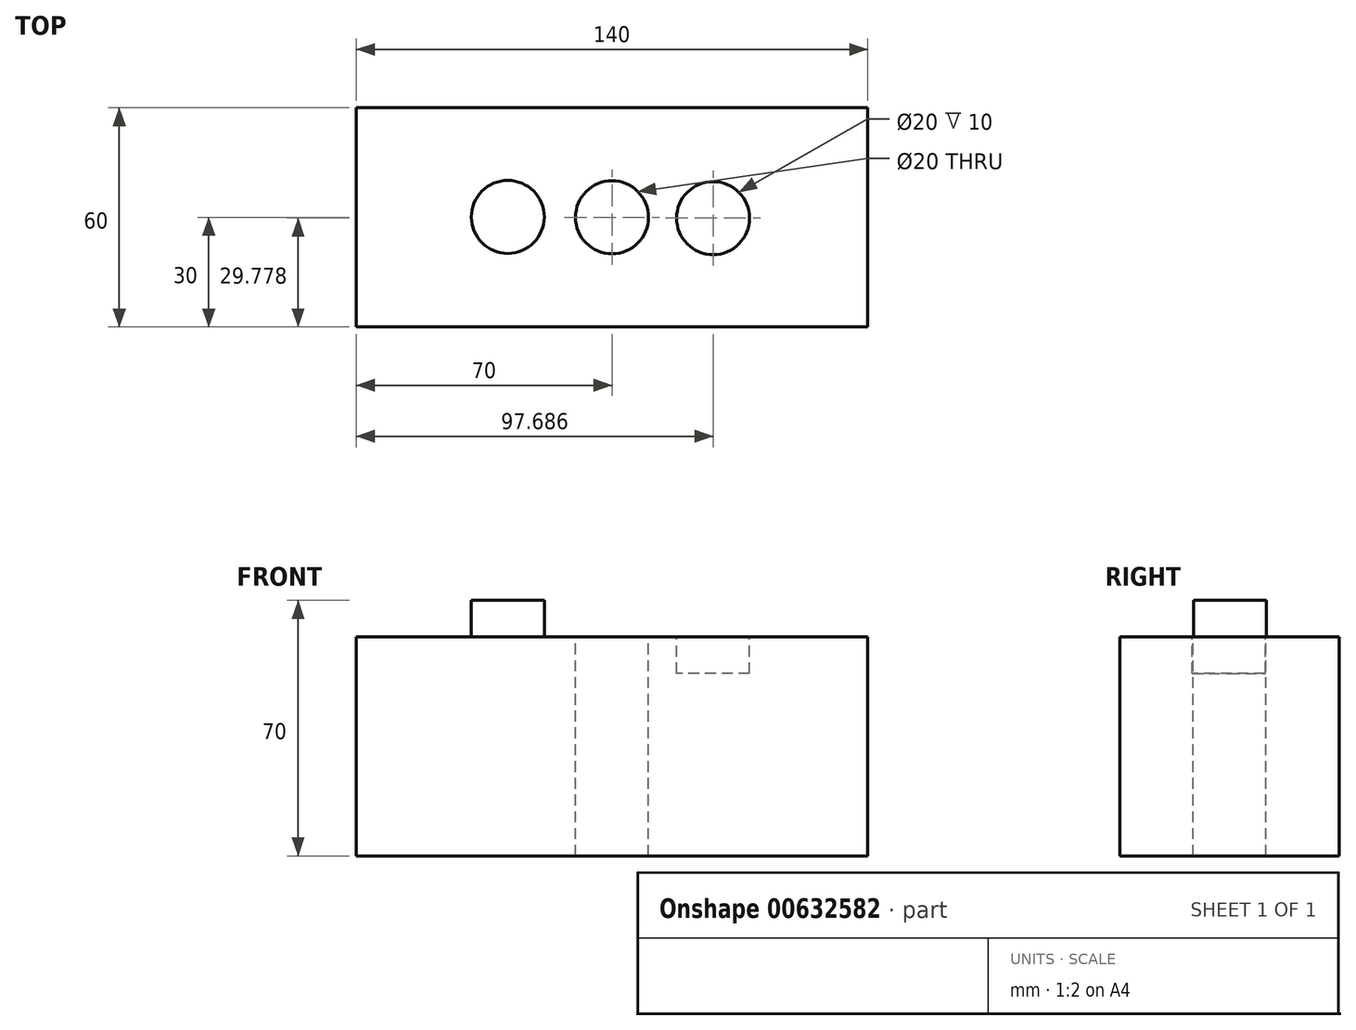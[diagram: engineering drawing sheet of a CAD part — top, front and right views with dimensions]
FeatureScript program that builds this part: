
annotation { "Feature Type Name" : "Feature", "Feature Type Description" : "" }
export const myFeature = defineFeature(function(context is Context, id is Id, definition is map)
    precondition{}
    {
        {
            var Q0;
            Q0=qCreatedBy(makeId("Top.planeOp"),FACE);
            var sketch = newSketch(context, id + "F0", { "sketchPlane" : qUnion([Q0])});
            skLineSegment(sketch, "E0.bottom", {"start": v(-70, 30) * mm, "end": v(70, 30) * mm});
            skLineSegment(sketch, "E0.top", {"start": v(-70, -30) * mm, "end": v(70, -30) * mm});
            skLineSegment(sketch, "E0.left", {"start": v(-70, 30) * mm, "end": v(-70, -30) * mm});
            skLineSegment(sketch, "E0.right", {"start": v(70, 30) * mm, "end": v(70, -30) * mm});
            skPoint(sketch, "E0.middle", {"position": v(0, 0) * mm});
            skSolve(sketch);
        }
        {
            var Q0;
            Q0 = qSketchRegion(id + "F0", true);
            extrude(context, id + "F1", {"entities" : qUnion([Q0]), "depth" : 60 * mm, "offsetDistance" : 25 * mm});
        }
        {
            var Q0;
            Q0=makeQuery(id+"F1.opExtrude","CAP_FACE",FACE,{"disambiguationData":[OSD([sQuery(id+"F0.wireOp",EDGE,"E0.bottom"),sQuery(id+"F0.wireOp",EDGE,"E0.top"),sQuery(id+"F0.wireOp",EDGE,"E0.left"),sQuery(id+"F0.wireOp",EDGE,"E0.right")])],"isStart":false});
            var sketch = newSketch(context, id + "F2", { "sketchPlane" : qUnion([Q0])});
            skLineSegment(sketch, "E1", {"start": v(-70, 0) * mm, "end": v(-49.87, 0) * mm});
            skPoint(sketch, "E1.endSnap0", {"position": v(-70, 0) * mm});
            skLineSegment(sketch, "E2", {"start": v(70, 0) * mm, "end": v(49, 0) * mm});
            skPoint(sketch, "E2.endSnap0", {"position": v(70, 0) * mm});
            skSolve(sketch);
        }
        {
            var Q0;
            {var subQ3=makeQuery(id+"F1.opExtrude","CAP_EDGE",EDGE,{"disambiguationData":[OSD([sQuery(id+"F0.wireOp",EDGE,"E0.bottom")])],"isStart":false});Q0=makeQuery(id+"F2.imprint","IMPRINT",FACE,{"disambiguationData":[TD([[makeQuery(id+"F2.imprint","IMPRINT",EDGE,{"derivedFrom":subQ3}),-1.0]])]});}
            var sketch = newSketch(context, id + "F3", { "sketchPlane" : qUnion([Q0])});
            skCircle(sketch, "E3", {"center": v(-28.55, 0.11) * mm, "radius": 10 * mm});
            skPoint(sketch, "E3.first.point", {"position": v(-38.55, 0) * mm});
            skPoint(sketch, "E3.second.point", {"position": v(-18.55, 0) * mm});
            skPoint(sketch, "E3.third.point", {"position": v(-28.78, 10.11) * mm});
            skSolve(sketch);
        }
        {
            var Q0;
            {var subQ3=makeQuery(id+"F1.opExtrude","CAP_EDGE",EDGE,{"disambiguationData":[OSD([sQuery(id+"F0.wireOp",EDGE,"E0.bottom")])],"isStart":false});Q0=makeQuery(id+"F2.imprint","IMPRINT",FACE,{"disambiguationData":[TD([[makeQuery(id+"F2.imprint","IMPRINT",EDGE,{"derivedFrom":subQ3}),-1.0]])]});}
            var sketch = newSketch(context, id + "F4", { "sketchPlane" : qUnion([Q0])});
            skCircle(sketch, "E4", {"center": v(27.69, -0.22) * mm, "radius": 10 * mm});
            skPoint(sketch, "E4.first.point", {"position": v(37.68, 0) * mm});
            skPoint(sketch, "E4.second.point", {"position": v(17.69, 0) * mm});
            skPoint(sketch, "E4.third.point", {"position": v(27.8, 9.78) * mm});
            skSolve(sketch);
        }
        {
            var Q0;
            {var subQ3=makeQuery(id+"F1.opExtrude","CAP_EDGE",EDGE,{"disambiguationData":[OSD([sQuery(id+"F0.wireOp",EDGE,"E0.bottom")])],"isStart":false});Q0=makeQuery(id+"F2.imprint","IMPRINT",FACE,{"disambiguationData":[TD([[makeQuery(id+"F2.imprint","IMPRINT",EDGE,{"derivedFrom":subQ3}),-1.0]])]});}
            var sketch = newSketch(context, id + "F5", { "sketchPlane" : qUnion([Q0])});
            skCircle(sketch, "E5", {"center": v(0, 0) * mm, "radius": 10 * mm});
            skSolve(sketch);
        }
        {
            var Q0;
            Q0 = qSketchRegion(id + "F3", true);
            extrude(context, id + "F6", {"entities" : qUnion([Q0]), "operationType" : NewBodyOperationType.ADD, "depth" : 10 * mm, "offsetDistance" : 25 * mm});
        }
        {
            var Q0;
            Q0 = qSketchRegion(id + "F4", true);
            extrude(context, id + "F7", {"entities" : qUnion([Q0]), "operationType" : NewBodyOperationType.REMOVE, "oppositeDirection" : true, "depth" : 10 * mm, "offsetDistance" : 25 * mm});
        }
        {
            var Q0;
            Q0 = qSketchRegion(id + "F5", true);
            extrude(context, id + "F8", {"entities" : qUnion([Q0]), "operationType" : NewBodyOperationType.REMOVE, "oppositeDirection" : true, "depth" : 72.9 * mm, "offsetDistance" : 25 * mm});
        }
    });
